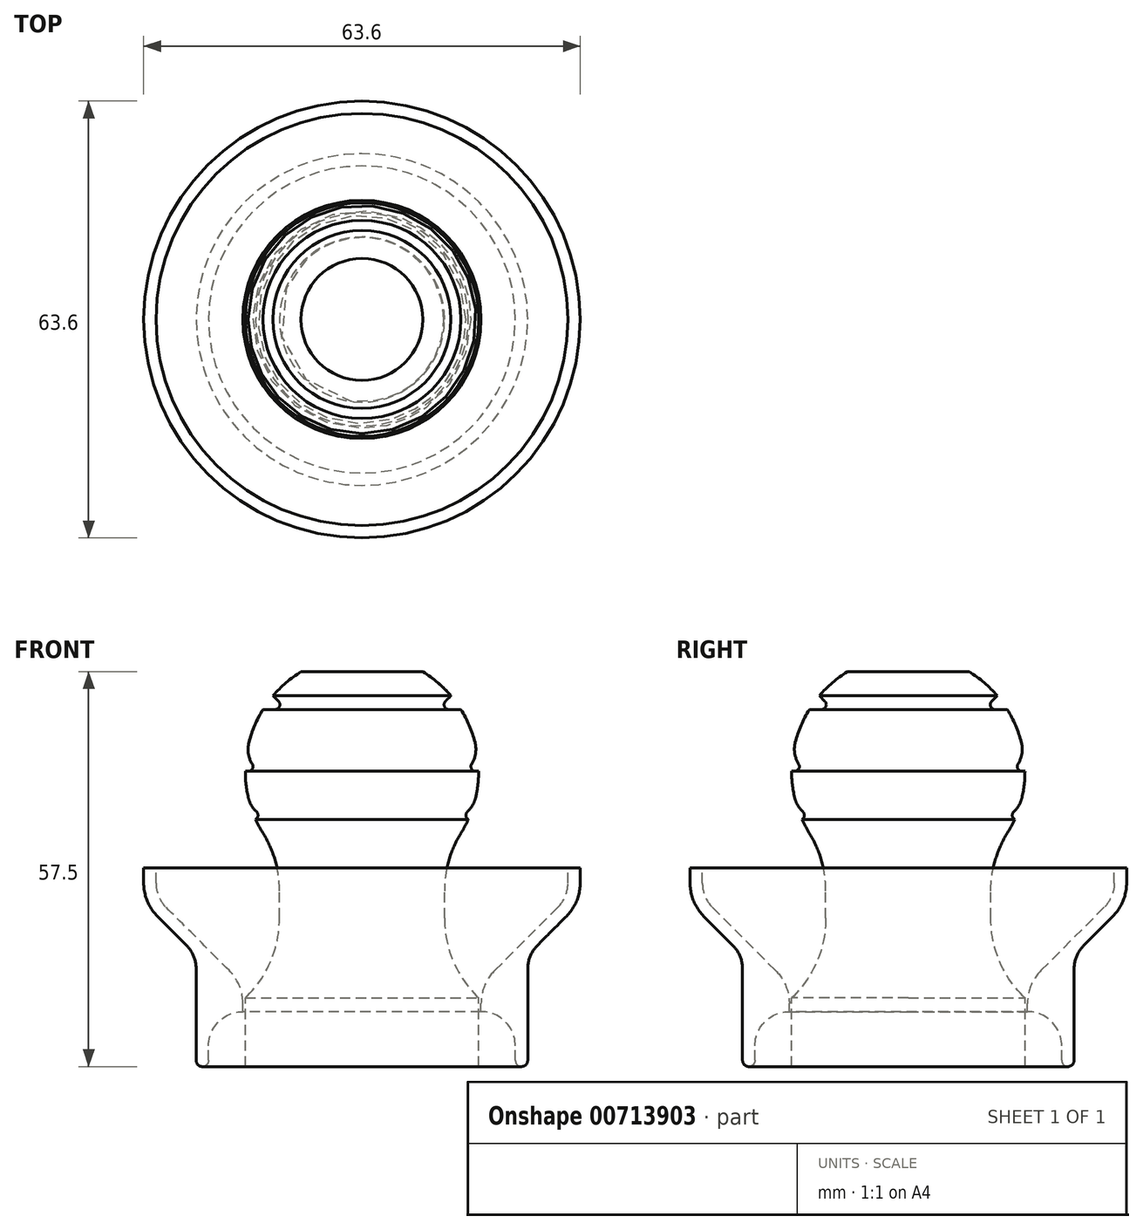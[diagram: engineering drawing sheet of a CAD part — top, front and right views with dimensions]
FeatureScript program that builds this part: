
annotation { "Feature Type Name" : "Feature", "Feature Type Description" : "" }
export const myFeature = defineFeature(function(context is Context, id is Id, definition is map)
    precondition{}
    {
        {
            assignVariable(context, id + "F0", {"name" : "Wall_Thickness", "anyValue" : 1.8});
        }
        {
            var Q0;
            Q0=qCreatedBy(makeId("Front.planeOp"),FACE);
            var sketch = newSketch(context, id + "F1", { "sketchPlane" : qUnion([Q0])});
            skLineSegment(sketch, "E0", {"start": v(0, 219.6) * mm, "end": v(0, -207.16) * mm, "construction": true});
            skLineSegment(sketch, "E1", {"start": v(-30, 24.65) * mm, "end": v(-17.35, 12) * mm});
            skLineSegment(sketch, "E2", {"start": v(-17.35, 12) * mm, "end": v(-17.35, 8) * mm});
            skLineSegment(sketch, "E3", {"start": v(-17.35, 8) * mm, "end": v(-22.35, 8) * mm});
            skLineSegment(sketch, "E4", {"start": v(-22.35, 8) * mm, "end": v(-22.35, 0) * mm});
            skLineSegment(sketch, "E5", {"start": v(-22.35, 0) * mm, "end": v(-24.15, 0) * mm});
            skLineSegment(sketch, "E6", {"start": v(-24.15, 0) * mm, "end": v(-24.15, 16.25) * mm});
            skLineSegment(sketch, "E7", {"start": v(-24.15, 16.25) * mm, "end": v(-31.8, 23.9) * mm});
            skLineSegment(sketch, "E8", {"start": v(-30, 24.65) * mm, "end": v(-30, 28.9) * mm});
            skLineSegment(sketch, "E9", {"start": v(-30, 28.9) * mm, "end": v(-31.8, 28.9) * mm});
            skLineSegment(sketch, "E10", {"start": v(-31.8, 28.9) * mm, "end": v(-31.8, 23.9) * mm});
            skSolve(sketch);
        }
        {
            var Q0;
            Q0=makeQuery(id+"F1.imprint","IMPRINT",FACE,{"disambiguationData":[TD([[makeQuery(id+"F1.imprint","IMPRINT",EDGE,{"derivedFrom":sQuery(id+"F1.wireOp",EDGE,"E1")}),-1.0]])]});
            var Q1;
            Q1=sQuery(id+"F1.wireOp",EDGE,"E0");
            revolve(context, id + "F2", {"surfaceOperationType" : NewSurfaceOperationType.NEW, "entities" : qUnion([Q0]), "axis" : qUnion([Q1]), "revolveType" : RevolveType.FULL});
        }
        {
            var Q0;
            Q0=makeQuery(id+"F2.opRevolve","SWEPT_EDGE",EDGE,{"disambiguationData":[OSD([sQuery(id+"F1.wireOp",EDGE,"E1"),sQuery(id+"F1.wireOp",EDGE,"E8")])]});
            var Q1;
            Q1=makeQuery(id+"F2.opRevolve","SWEPT_EDGE",EDGE,{"disambiguationData":[OSD([sQuery(id+"F1.wireOp",EDGE,"E6"),sQuery(id+"F1.wireOp",EDGE,"E7")])]});
            fillet(context, id + "F3", {"entities" : qUnion([Q0, Q1]), "radius" : 5 * mm, "tangentPropagation" : true, "allowEdgeOverflow" : false});
        }
        {
            var Q0;
            Q0=makeQuery(id+"F2.opRevolve","SWEPT_EDGE",EDGE,{"disambiguationData":[OSD([sQuery(id+"F1.wireOp",EDGE,"E3"),sQuery(id+"F1.wireOp",EDGE,"E4")])]});
            fillet(context, id + "F4", {"entities" : qUnion([Q0]), "radius" : 5 * mm, "tangentPropagation" : true, "allowEdgeOverflow" : false});
        }
        {
            var Q0;
            Q0=makeQuery(id+"F2.opRevolve","SWEPT_EDGE",EDGE,{"disambiguationData":[OSD([sQuery(id+"F1.wireOp",EDGE,"E7"),sQuery(id+"F1.wireOp",EDGE,"E10")])]});
            var Q1;
            Q1=makeQuery(id+"F2.opRevolve","SWEPT_EDGE",EDGE,{"disambiguationData":[OSD([sQuery(id+"F1.wireOp",EDGE,"E1"),sQuery(id+"F1.wireOp",EDGE,"E2")])]});
            fillet(context, id + "F5", {"entities" : qUnion([Q0, Q1]), "radius" : (5 + getVariable(context, 'Wall_Thickness')) * mm, "tangentPropagation" : true, "allowEdgeOverflow" : false});
        }
        {
            var Q0;
            Q0=makeQuery(id+"F2.opRevolve","SWEPT_FACE",FACE,{"disambiguationData":[OSD([sQuery(id+"F1.wireOp",EDGE,"E5")])]});
            fillet(context, id + "F6", {"entities" : qUnion([Q0]), "radius" : (getVariable(context, 'Wall_Thickness') / 2) * mm, "tangentPropagation" : true, "allowEdgeOverflow" : false});
        }
        {
            var Q0;
            Q0=qCreatedBy(makeId("Front.planeOp"),FACE);
            var sketch = newSketch(context, id + "F7", { "sketchPlane" : qUnion([Q0])});
            skLineSegment(sketch, "E11", {"start": v(0, 94.6) * mm, "end": v(0, -14.77) * mm, "construction": true});
            skLineSegment(sketch, "E12", {"start": v(0, 0) * mm, "end": v(-17, 0) * mm});
            skLineSegment(sketch, "E13", {"start": v(-17, 0) * mm, "end": v(-17, 10) * mm});
            skLineSegment(sketch, "E14", {"start": v(-17, 10) * mm, "end": v(-12.02, 14.98) * mm});
            skLineSegment(sketch, "E15", {"start": v(-12.02, 14.98) * mm, "end": v(-12.02, 30.98) * mm});
            skArc(sketch, "E16", {"start": v(-12.02, 30.98) * mm, "mid": v(-15.7, 49.5) * mm, "end": v(0, 60) * mm});
            skLineSegment(sketch, "E17", {"start": v(0, 60) * mm, "end": v(0, 0) * mm});
            skLineSegment(sketch, "E18", {"start": v(-12.02, 30.98) * mm, "end": v(0, 18.96) * mm, "construction": true});
            skSolve(sketch);
        }
        {
            var Q0;
            Q0 = qSketchRegion(id + "F7", true);
            var Q1;
            Q1=sQuery(id+"F7.wireOp",EDGE,"E17");
            revolve(context, id + "F8", {"surfaceOperationType" : NewSurfaceOperationType.NEW, "entities" : qUnion([Q0]), "axis" : qUnion([Q1]), "revolveType" : RevolveType.FULL});
        }
        {
            var Q0;
            Q0=makeQuery(id+"F8.opRevolve","SWEPT_FACE",FACE,{"disambiguationData":[OSD([sQuery(id+"F7.wireOp",EDGE,"E15")])]});
            fillet(context, id + "F9", {"entities" : qUnion([Q0]), "radius" : 16 * mm, "tangentPropagation" : true, "allowEdgeOverflow" : false});
        }
        {
            var Q0;
            Q0=qCreatedBy(makeId("Front.planeOp"),FACE);
            var sketch = newSketch(context, id + "F10", { "sketchPlane" : qUnion([Q0])});
            skArc(sketch, "E19", {"start": v(14.43, 34.02) * mm, "mid": v(0, 60) * mm, "end": v(-14.43, 34.02) * mm});
            skArc(sketch, "E20", {"start": v(14.43, 34.02) * mm, "mid": v(12.64, 29.96) * mm, "end": v(12.02, 25.57) * mm});
            skLineSegment(sketch, "E21", {"start": v(12.02, 25.57) * mm, "end": v(12.02, 21.6) * mm});
            skArc(sketch, "E22", {"start": v(12.02, 21.6) * mm, "mid": v(13.24, 15.48) * mm, "end": v(16.7, 10.3) * mm});
            skLineSegment(sketch, "E23", {"start": v(12.96, 54) * mm, "end": v(10.96, 52) * mm});
            skLineSegment(sketch, "E24", {"start": v(10.96, 52) * mm, "end": v(14.42, 52) * mm});
            skLineSegment(sketch, "E25", {"start": v(16.88, 45) * mm, "end": v(14.88, 43) * mm});
            skLineSegment(sketch, "E26", {"start": v(14.88, 43) * mm, "end": v(17, 43) * mm});
            skLineSegment(sketch, "E27", {"start": v(16.25, 38) * mm, "end": v(14.25, 36) * mm});
            skLineSegment(sketch, "E28", {"start": v(14.25, 36) * mm, "end": v(15.5, 36) * mm});
            skLineSegment(sketch, "E29", {"start": v(0, 54.18) * mm, "end": v(0, 36.85) * mm, "construction": true});
            skArc(sketch, "E30", {"start": v(12.96, 54) * mm, "mid": v(13.73, 53.03) * mm, "end": v(14.42, 52) * mm});
            skArc(sketch, "E31", {"start": v(16.88, 45) * mm, "mid": v(16.97, 44) * mm, "end": v(17, 43) * mm});
            skArc(sketch, "E32", {"start": v(16.25, 38) * mm, "mid": v(15.9, 36.99) * mm, "end": v(15.5, 36) * mm});
            skSolve(sketch);
        }
        {
            var Q0;
            Q0 = qSketchRegion(id + "F10", true);
            var Q1;
            Q1=sQuery(id+"F10.wireOp",EDGE,"TTvGmyuC-54k7-2YPy-VsrL-iChz2TTG4EuJ");
            var Q2;
            Q2=sQuery(id+"F10.wireOp",EDGE,"E23");
            var Q3;
            Q3=sQuery(id+"F10.wireOp",EDGE,"E24");
            var Q4;
            Q4=sQuery(id+"F10.wireOp",EDGE,"E30");
            var Q5;
            Q5=sQuery(id+"F10.wireOp",EDGE,"E29");
            revolve(context, id + "F11", {"operationType" : NewBodyOperationType.REMOVE, "surfaceOperationType" : NewSurfaceOperationType.NEW, "entities" : qUnion([Q0]), "surfaceEntities" : qUnion([Q1, Q2, Q3, Q4]), "axis" : qUnion([Q5]), "revolveType" : RevolveType.FULL});
        }
        {
            var Q0;
            Q0=makeQuery(id+"F11.boolean.opBoolean","COPY",EDGE,{"derivedFrom":makeQuery(id+"F11.opRevolve","SWEPT_EDGE",EDGE,{"disambiguationData":[OSD([sQuery(id+"F10.wireOp",EDGE,"E27"),sQuery(id+"F10.wireOp",EDGE,"E28")])]})});
            var Q1;
            Q1=makeQuery(id+"F11.boolean.opBoolean","COPY",EDGE,{"derivedFrom":makeQuery(id+"F11.opRevolve","SWEPT_EDGE",EDGE,{"disambiguationData":[OSD([sQuery(id+"F10.wireOp",EDGE,"E23"),sQuery(id+"F10.wireOp",EDGE,"E24")])]})});
            var Q2;
            Q2=makeQuery(id+"F11.boolean.opBoolean","COPY",EDGE,{"derivedFrom":makeQuery(id+"F11.opRevolve","SWEPT_EDGE",EDGE,{"disambiguationData":[OSD([sQuery(id+"F10.wireOp",EDGE,"E25"),sQuery(id+"F10.wireOp",EDGE,"E26")])]})});
            fillet(context, id + "F12", {"entities" : qUnion([Q0, Q1, Q2]), "radius" : .7 * mm, "tangentPropagation" : true, "allowEdgeOverflow" : false});
        }
        {
            var Q0;
            Q0=makeQuery(id+"F11.boolean.opBoolean","COPY",EDGE,{"derivedFrom":makeQuery(id+"F11.opRevolve","SWEPT_EDGE",EDGE,{"disambiguationData":[OSD([sQuery(id+"F10.wireOp",EDGE,"E23"),sQuery(id+"F10.wireOp",EDGE,"E30")])]})});
            var Q1;
            Q1=makeQuery(id+"F11.boolean.opBoolean","COPY",EDGE,{"derivedFrom":makeQuery(id+"F11.opRevolve","SWEPT_EDGE",EDGE,{"disambiguationData":[OSD([sQuery(id+"F10.wireOp",EDGE,"E25"),sQuery(id+"F10.wireOp",EDGE,"E31")])]})});
            var Q2;
            Q2=makeQuery(id+"F11.boolean.opBoolean","COPY",EDGE,{"derivedFrom":makeQuery(id+"F11.opRevolve","SWEPT_EDGE",EDGE,{"disambiguationData":[OSD([sQuery(id+"F10.wireOp",EDGE,"E27"),sQuery(id+"F10.wireOp",EDGE,"E32")])]})});
            fillet(context, id + "F13", {"entities" : qUnion([Q0, Q1, Q2]), "radius" : 4 * mm, "tangentPropagation" : true, "allowEdgeOverflow" : false});
        }
        {
            var Q0;
            Q0=qCreatedBy(makeId("Top.planeOp"),FACE);
            cPlane(context, id + "F14", {"entities" : qUnion([Q0]), "cplaneType" : CPlaneType.OFFSET, "offset" : 61 * mm, "width" : 150 * mm, "height" : 150 * mm});
        }
        {
            var Q0;
            Q0=qCreatedBy(id+"F14.planeOp",FACE);
            var sketch = newSketch(context, id + "F15", { "sketchPlane" : qUnion([Q0])});
            skLineSegment(sketch, "E33.bottom", {"start": v(-17.5, 17.5) * mm, "end": v(17.5, 17.5) * mm});
            skLineSegment(sketch, "E33.top", {"start": v(-17.5, -17.5) * mm, "end": v(17.5, -17.5) * mm});
            skLineSegment(sketch, "E33.left", {"start": v(-17.5, 17.5) * mm, "end": v(-17.5, -17.5) * mm});
            skLineSegment(sketch, "E33.right", {"start": v(17.5, 17.5) * mm, "end": v(17.5, -17.5) * mm});
            skSolve(sketch);
        }
        {
            var Q0;
            Q0=makeQuery(id+"F15.imprint","IMPRINT",FACE,{"disambiguationData":[TD([[makeQuery(id+"F15.imprint","IMPRINT",EDGE,{"derivedFrom":sQuery(id+"F15.wireOp",EDGE,"E33.bottom")}),-1.0]])]});
            extrude(context, id + "F16", {"entities" : qUnion([Q0]), "operationType" : NewBodyOperationType.REMOVE, "oppositeDirection" : true, "depth" : 3.5 * mm, "offsetDistance" : 25 * mm});
        }
    });
